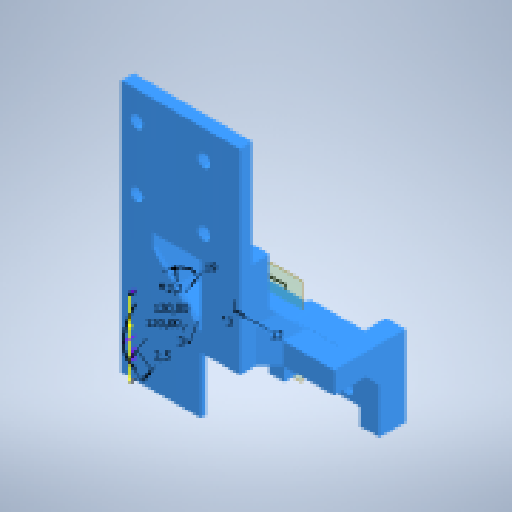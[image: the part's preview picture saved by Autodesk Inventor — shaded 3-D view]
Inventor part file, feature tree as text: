
AUTODESK INVENTOR PART (.ipt)
format: ipt  version: 2024.2 (Build 282272000, 272)  size: 638,464 bytes
history: native  units: mm
features: sketch x25, chamfer x25, extrude x24, other x11, projected_geometry x4, reference x1
ambient origin geometry x8: Origin, YZ Plane, XZ Plane, XY Plane, X Axis, Y Axis, Z Axis, Center Point
bodies: Body1 (feature_tree)
feature tree (90):
  other  "Твердое тело1"
  extrude  "Выдавливание1"  Depth=8.0mm
  sketch  "Эскиз2"
  sketch  "Эскиз3"
  extrude  "Выдавливание3"  Depth=6.0mm TaperAngle=0.0deg
  extrude  "Выдавливание4"  Depth=4.0mm
  extrude  "Выдавливание2"  Depth=4.0mm
  other  "РабПлоскость2"
  sketch  "Эскиз5"
  extrude  "Выдавливание5"  Depth=10.0mm
  other  "РабПлоскость4"
  other  "РабПлоскость5"
  extrude  "Выдавливание14"  Depth=2.0mm
  other  "РабПлоскость6"
  sketch  "Эскиз17"
  extrude  "Выдавливание15"  Depth=8.0mm
  chamfer  "Фаска6"  Distance=12.0mm
  extrude  "Выдавливание16"  Depth=2.0mm
  chamfer  "Фаска7"  Distance=2.0mm
  extrude  "Выдавливание17"  Depth=1.0mm
  extrude  "Выдавливание18"  Depth=1.0mm
  chamfer  "Фаска8"  Distance=2.0mm
  sketch  "Эскиз23"
  other  "РабПлоскость7"
  chamfer  "Фаска3"  [1 undecoded]
  extrude  "Выдавливание21"  Depth=12.0mm
  extrude  "Выдавливание23"  Depth=8.0mm
  extrude  "Выдавливание24"  Depth=3.0mm
  extrude  "Выдавливание25"  Depth=19.0mm
  chamfer  "Фаска16"  Distance=2.2mm
  extrude  "Выдавливание26"  Depth=3.0mm
  chamfer  "Фаска17"  Distance=3.0mm
  chamfer  "Фаска18"  Distance=3.0mm
  chamfer  "Фаска20"  Distance=9.0mm
  sketch  "Эскиз31"
  extrude  "Выдавливание27"  Depth=10.0mm TaperAngle=0.0deg
  extrude  "Выдавливание28"  Depth=1.0mm
  chamfer  "Фаска21"  Distance=1.0mm
  chamfer  "Фаска22"  Distance=13.0mm
  chamfer  "Фаска23"  Distance=10.0mm
  extrude  "Выдавливание29"  Depth=5.0mm TaperAngle=45.0deg
  extrude  "Выдавливание30"  Depth=12.0mm
  extrude  "Выдавливание31"  Depth=3.0mm
  chamfer  "Фаска24"  Distance=13.0mm
  chamfer  "Фаска25"  Distance=10.0mm
  extrude  "Выдавливание32"  Depth=10.0mm TaperAngle=0.0deg
  chamfer  "Фаска26"  Distance=18.0mm Angle=45.0deg
  sketch  "Эскиз37"
  chamfer  "Фаска27"  Distance=14.0mm
  chamfer  "Фаска28"  Distance=5.6mm
  chamfer  "Фаска29"  Distance=13.0mm
  chamfer  "Фаска30"  Distance=2.0mm Angle=45.0deg
  chamfer  "Фаска31"  Distance=5.5mm
  chamfer  "Фаска32"  Distance=7.0mm
  extrude  "Выдавливание33"  TaperAngle=0.0deg  [1 undecoded]
  chamfer  "Фаска33"  Distance=5.0mm
  extrude  "Выдавливание34"  Depth=1.514mm TaperAngle=45.0deg
  chamfer  "Фаска34"  Distance=3.029555mm
  chamfer  "Фаска35"  Distance=18.0mm
  extrude  "Выдавливание35"  Depth=2.5mm
  chamfer  "Фаска36"  Distance=2.5mm
  chamfer  "Фаска37"  Distance=7.0mm
  sketch  "Эскиз1"
  projected_geometry  "Спроецированная петля1"
  sketch  "Эскиз4"
  other  "РабПлоскость1"
  sketch  "Эскиз16"
  sketch  "Эскиз18"
  sketch  "Эскиз19"
  sketch  "Эскиз25"
  sketch  "Эскиз27"
  sketch  "Эскиз28"
  projected_geometry  "Спроецированная петля6"
  projected_geometry  "Спроецированная петля7"
  sketch  "Эскиз29"
  projected_geometry  "Спроецированная петля8"
  sketch  "Эскиз30"
  reference  "Ссылка10"
  sketch  "Эскиз32"
  sketch  "Эскиз33"
  sketch  "Эскиз34"
  sketch  "Эскиз35"
  sketch  "Эскиз36"
  sketch  "Эскиз38"
  sketch  "Эскиз39"
  sketch  "Эскиз40"
  other  "<userpath>\Documents\Artist-v2\3D\каретка.iam"
  other  "каретка.iam"
  other  "Сервопривод:1"
  other  "Проецирование ребер1"
note: 2 required parameter values undecoded (feature->parameter linkage not recoverable at this tier; creation-order binding heuristic only, values carry confidence <= 0.55)
